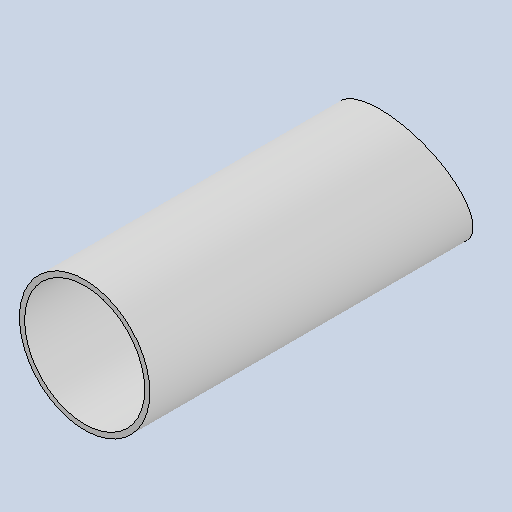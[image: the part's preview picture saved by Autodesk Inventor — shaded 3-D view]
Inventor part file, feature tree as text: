
AUTODESK INVENTOR PART (.ipt)
format: ipt  version: 2025 (Build 290162010, 162A)  size: 105,472 bytes
history: native  units: mm
features: extrude x2, sketch x2, projected_geometry x1
ambient origin geometry x8: Origin, YZ Plane, XZ Plane, XY Plane, X Axis, Y Axis, Z Axis, Center Point
bodies: Solid1 (feature_tree)
feature tree (5):
  extrude  "Extrusion1"  Depth=3.0mm
  extrude  "Extrusion2"  Depth=200.0mm
  sketch  "Sketch1"  dims[d0=76.1mm d1=3.0mm]
  sketch  "Sketch2"  dims[d2=200.0mm d3=0.0mm d4=3.490659mm d5=300.0mm d6=0.0mm]
  projected_geometry  "Projected Loop1"
